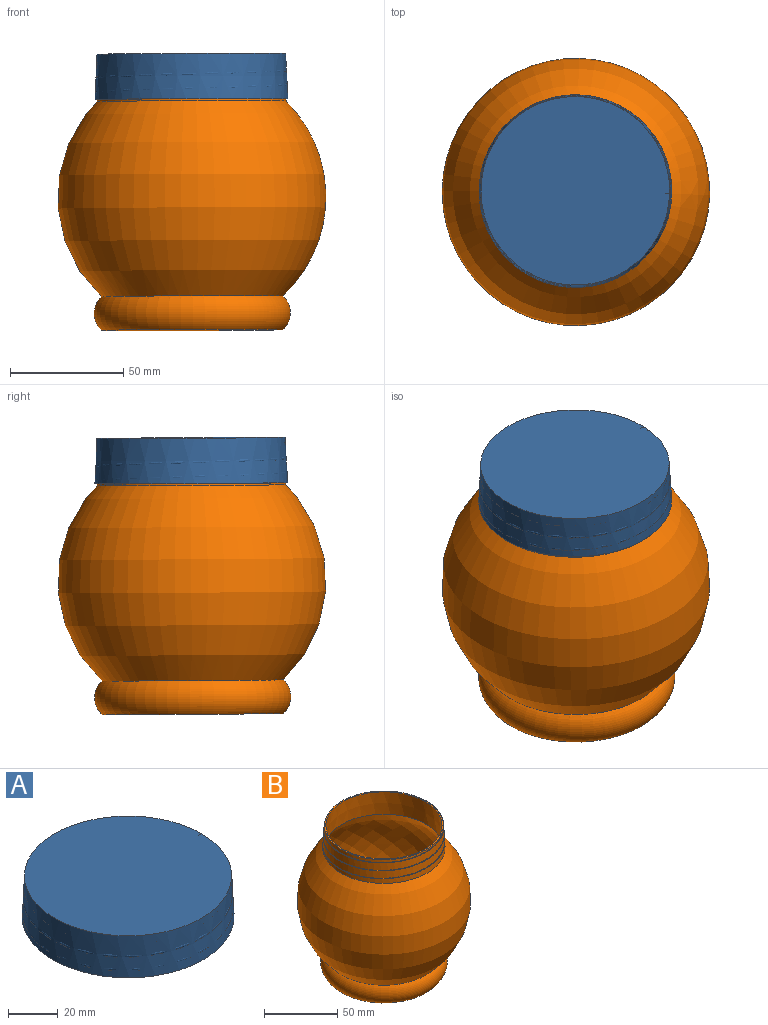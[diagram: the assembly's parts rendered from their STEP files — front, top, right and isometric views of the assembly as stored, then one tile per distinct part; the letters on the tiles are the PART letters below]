
ASSEMBLY  parts=2 mates=1
PART A: 9 faces, bbox 85.6x85.6x21.4 mm
  f0: cone r=0mm half-angle=89.8deg, axis (0,0,1), area 5175.7mm2, adj f1,f5,f7
  f1: cone r=40.69mm half-angle=2.7deg, axis (0,0,-1), area 3525.6mm2, adj f0,f2,f5,f6,f7,f8
  f2: cone r=41.59mm half-angle=87.3deg, axis (0,0,1), area 232.2mm2, adj f1,f3,f6,f8
  f3: cone r=42.59mm half-angle=2.7deg, axis (0,0,-1), area 5292.5mm2, adj f2,f4
  f4: plane 83.29x83.29mm, normal (0,0,1), area 5448.8mm2, adj f3
  f5: plane 2.28x2.28mm, normal (0,-1,0), area 1.7mm2, adj f0,f1,f7
  f6: plane 1.22x1.11mm, normal (0,1,0), area 0.7mm2, adj f1,f2,f7
  f7: bspline ~84.84x84.53mm, area 2188.3mm2, adj f0,f1,f5,f6
  f8: bspline ~84.84x84.53mm, area -135.7mm2, adj f1,f2
PART B: 12 faces, bbox 118.5x118.5x122.8 mm
  f0: cone r=40.6mm half-angle=3.2deg, axis (0,0,-1), area 4638.3mm2, adj f1,f4,f9,f10,f11
  f1: plane 81.27x81.27mm, normal (0,0,1), area 251.4mm2, adj f0,f5,f9,f11
  f2: plane 80x80mm, normal (0,0,-1), area 5026.5mm2, adj f3
  f3: torus R=33.31mm, axis (0,0,-1), area 4441mm2, adj f2,f4
  f4: revolved ~118.41x118.41mm, area 32019.4mm2, adj f0,f3,f10,f11
  f5: cone r=39.6mm half-angle=3.2deg, axis (0,0,-1), area 4909.8mm2, adj f1,f8
  f6: plane 79.21x79.21mm, normal (0,0,1), area 4927.6mm2, adj f7
  f7: torus R=33.31mm, axis (0,0,-1), area 4093.2mm2, adj f6,f8
  f8: revolved ~116.39x116.39mm, area 31334.6mm2, adj f5,f7
  f9: plane 0.39x0.39mm, normal (0,1,0), area 0.1mm2, adj f0,f1,f11
  f10: plane 0.36x0.25mm, normal (0,-1,0), area 0mm2, adj f0,f4,f11
  f11: bspline ~83.4x83.1mm, area 411.2mm2, adj f0,f1,f4,f9,f10
PLACE A rot(axis=(-0.23,-0.14,-0.96),1.6deg) t=(-14.14,21.82,46.33)mm
PLACE B rot(axis=(-0.23,-0.14,-0.96),1.6deg) t=(-14.14,21.82,45.52)mm
MATE cylindrical A.f0 <-> B.f0  axis (0,0.01,1) through (-14.37,22.23,109.29)mm
